# Revit family: HL_Корпус плоского душевого лотка InFloor_HL53KF
name_source: partatom
category: Instalační zařizovací předměty
revit_build: Autodesk Revit 2016 (Build: 20151007_0715(x64)
units: mm (PartAtom-declared; Revit-internal decimal feet)

## family parameters
Bod výpočtu místnosti = Ano
Kóta kulaté spojky = Použít průměr
Nadpis OmniClass = General Pipework and Ductwork Products
Ořezat dutým tvarem při načtení = Ne
Sdílené = Ne
Typ součásti = Normální
Vždy vertikální = Ano
Založené na pracovní rovině = Ne
Číslo OmniClass = 23.60.30.00

## types (2) — shared parameters
E = HL_Решётка душевого лотка InFloor Стандарт_HL053S : HL_Решётка душевого лотка InFloor Стандарт_HL053S_90
F = HL_Решётка душевого лотка InFloor Стандарт_HL053S : HL_Решётка душевого лотка InFloor Стандарт_HL053S_100
G = HL_Решётка душевого лотка InFloor Стандарт_HL053S : HL_Решётка душевого лотка InFloor Стандарт_HL053S_120
H = HL_Решётка душевого лотка InFloor стандарт_HL053WS : HL_Решётка душевого лотка InFloor стандарт_HL053WS_90
HL052_тип = HL_Pешётка InFloor_HL052 : HL_Решётка душевого лотка InFloor матовая_HL052M
HL053_тип = HL_Решётка душевого лотка InFloor матовая_HL053M : HL_Решётка душевого лотка InFloor матовая_HL053M_80
I = HL_Решётка душевого лотка InFloor стандарт_HL053WS : HL_Решётка душевого лотка InFloor стандарт_HL053WS_100
J = HL_Решётка душевого лотка InFloor стандарт_HL053WS : HL_Решётка душевого лотка InFloor стандарт_HL053WS_120
Popis = Корпус плоского душевого лотка InFloor CeraDrain, DN40
URL = http://www.hutterer-lechner.com
Výrobce = HL Hutterer & Lechner GmbH
МАТЕРИАЛ = PP
НОМИНАЛЬНЫЙ ДИАМЕТР = 40 mm
ПРОИЗВОДИТЕЛЬНОСТЬ = 0,4l/s
ПРОПУСКНАЯ СПОСОБНОСТЬ = 0.0 m³/h
РАЗМЕР = DN40
zero-valued in all types: Cena

## per-type parameters (varying)
| type | BO | EAN | Klíčová poznámka | Komentáře k typům | Model | ВЕС | ВЫСОТА МОНТАЖА |
| HL_Корпус плоского душевого лотка InFloor_HL53KF | HL_53KF | 9003076041251 | HL53KF | Корпус плоского душевого лотка InFloor, DN40 | HL53KF | 1,25 kg | 65-143mm |
| HL_Корпус плоского душевого лотка InFloor_HL53KFC | HL_53KF : HL_53KFC | 9003076047826 | HL53KFC | Корпус плоского душевого лотка InFloor CeraDrain, DN40 | HL53KFC | 4,3 kg | 65-131mm |
